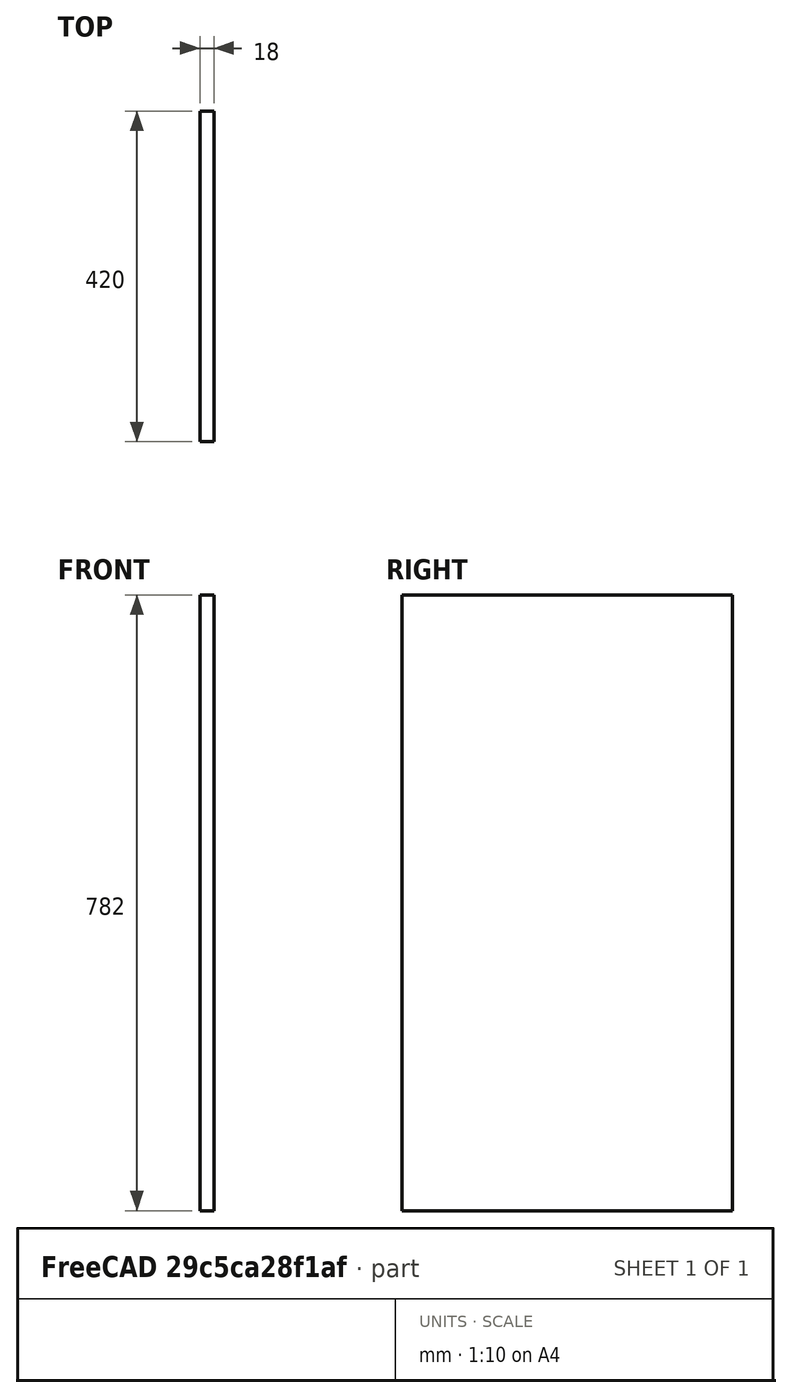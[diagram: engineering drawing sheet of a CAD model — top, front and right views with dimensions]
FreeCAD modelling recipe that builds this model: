
FCSTD DOCUMENT  (FreeCAD 0.18R4 (GitTag))
Label: back
License: All rights reserved
LicenseURL: http://en.wikipedia.org/wiki/All_rights_reserved
objects: Sketcher::SketchObject×1, PartDesign::Pad×1, PartDesign::Body×1
note: 4 computed .brp shape members not serialized (recipe doc carries the construction recipe); baked Part::Feature solids carry a one-line shape summary decoded from their .brp

FEATURE [Sketcher::SketchObject] Sketch
  MapMode = 5
  Placement = pos=(0,0,0) rot=(0.57735,0.57735,0.57735;2.0944rad)
  Support = -> [YZ_Plane]
  sketch-geometry (4):
    g0: LineSegment StartX=0 StartY=0 StartZ=0 EndX=-420 EndY=0 EndZ=0
    g1: LineSegment StartX=-420 StartY=0 StartZ=0 EndX=-420 EndY=782 EndZ=0
    g2: LineSegment StartX=-420 StartY=782 StartZ=0 EndX=0 EndY=782 EndZ=0
    g3: LineSegment StartX=0 StartY=782 StartZ=0 EndX=0 EndY=0 EndZ=0
  constraints (11):
    c: Coincident(g0,g1)
    c: Coincident(g1,g2)
    c: Coincident(g2,g3)
    c: Coincident(g3,g0)
    c: Horizontal(g0)
    c: Horizontal(g2)
    c: Vertical(g1)
    c: Vertical(g3)
    c: Coincident(g0,g-1)
    c: DistanceX(g0,g0) = 420
    c: DistanceY(g3,g3) = 782
FEATURE [PartDesign::Pad] Pad
  Length = 18
  Length2 = 100
  Placement = pos=(0,0,0) rot=(0.57735,0.57735,0.57735;2.0944rad)
  Profile = -> Sketch
  Type = 0
FEATURE [PartDesign::Body] Body
  Group = -> [Sketch,Pad]
  Origin = -> Origin
  Tip = -> Pad
